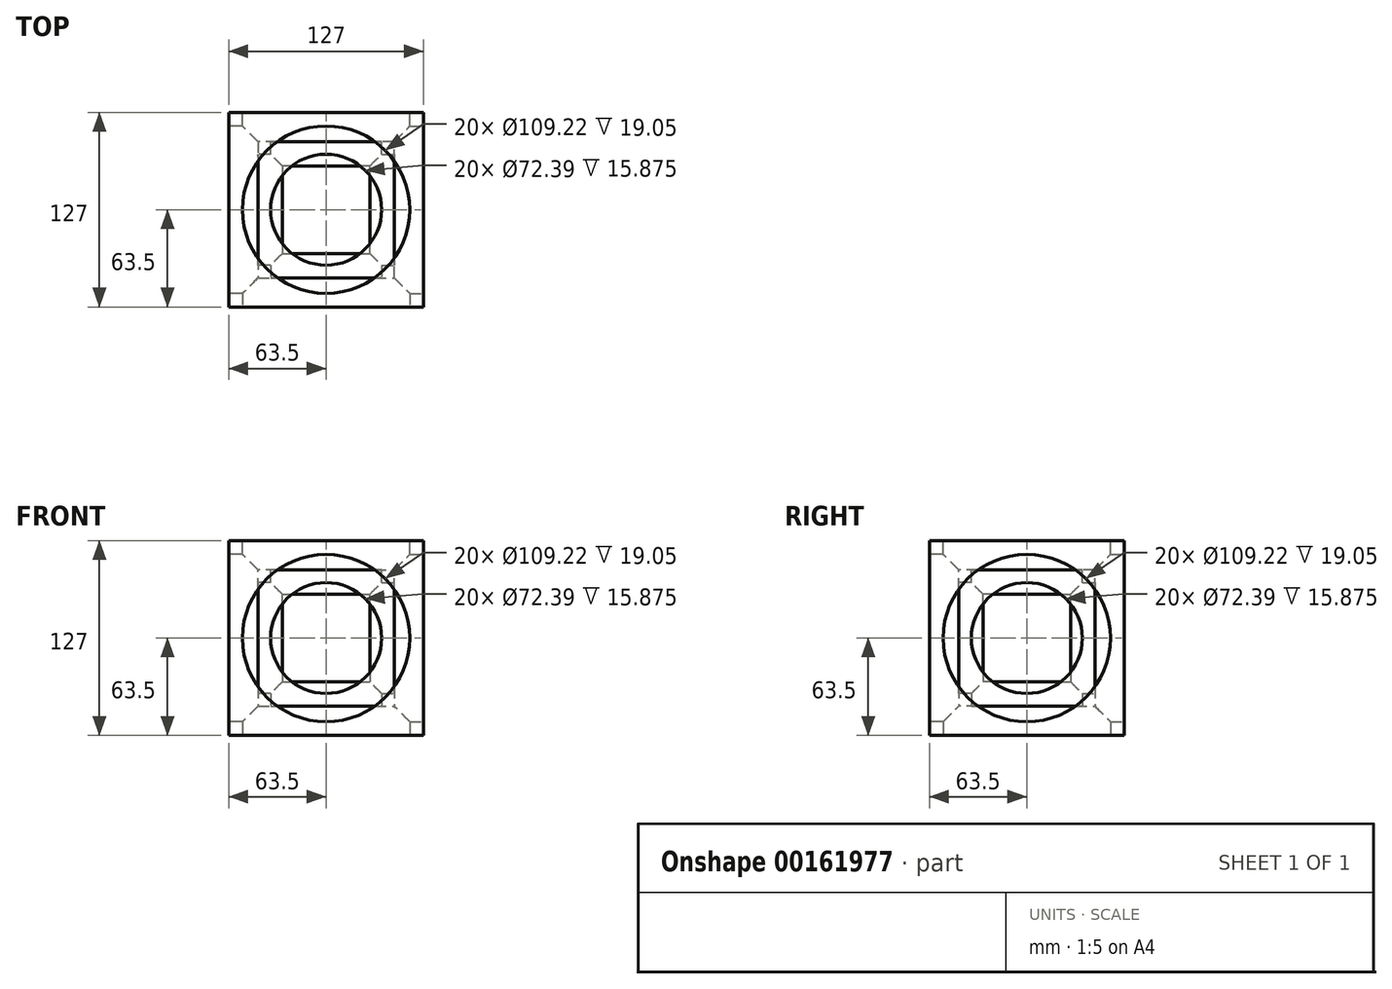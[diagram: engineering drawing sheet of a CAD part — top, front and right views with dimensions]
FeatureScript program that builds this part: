
annotation { "Feature Type Name" : "Feature", "Feature Type Description" : "" }
export const myFeature = defineFeature(function(context is Context, id is Id, definition is map)
    precondition{}
    {
        {
            var Q0;
            Q0=qCreatedBy(makeId("Top.planeOp"),FACE);
            var sketch = newSketch(context, id + "F15", { "sketchPlane" : qUnion([Q0])});
            skLineSegment(sketch, "E0.bottom", {"start": v(63.5, -63.5) * mm, "end": v(-63.5, -63.5) * mm});
            skLineSegment(sketch, "E0.top", {"start": v(63.5, 63.5) * mm, "end": v(-63.5, 63.5) * mm});
            skLineSegment(sketch, "E0.left", {"start": v(63.5, -63.5) * mm, "end": v(63.5, 63.5) * mm});
            skLineSegment(sketch, "E0.right", {"start": v(-63.5, -63.5) * mm, "end": v(-63.5, 63.5) * mm});
            skPoint(sketch, "E0.middle", {"position": v(0, 0) * mm});
            skSolve(sketch);
        }
        {
            var Q0;
            Q0=makeQuery(id+"F15.imprint","IMPRINT",FACE,{"disambiguationData":[TD([[makeQuery(id+"F15.imprint","IMPRINT",EDGE,{"derivedFrom":sQuery(id+"F15.wireOp",EDGE,"E0.bottom")}),-1.0]])]});
            extrude(context, id + "F16", {"entities" : qUnion([Q0]), "depth" : 127 * mm});
        }
        {
            var Q0;
            Q0=makeQuery(id+"F16.opExtrude","CAP_FACE",FACE,{"disambiguationData":[OSD([sQuery(id+"F15.wireOp",EDGE,"E0.bottom"),sQuery(id+"F15.wireOp",EDGE,"E0.top"),sQuery(id+"F15.wireOp",EDGE,"E0.left"),sQuery(id+"F15.wireOp",EDGE,"E0.right")])],"isStart":false});
            var sketch = newSketch(context, id + "F0", { "sketchPlane" : qUnion([Q0])});
            skCircle(sketch, "E1", {"center": v(0, 0) * mm, "radius": 54.61 * mm});
            skSolve(sketch);
        }
        {
            var Q0;
            Q0=makeQuery(id+"F0.imprint","IMPRINT",FACE,{"disambiguationData":[TD([[makeQuery(id+"F0.imprint","IMPRINT",EDGE,{"derivedFrom":sQuery(id+"F0.wireOp",EDGE,"E1")}),1.0]])]});
            extrude(context, id + "F17", {"entities" : qUnion([Q0]), "operationType" : NewBodyOperationType.REMOVE, "oppositeDirection" : true, "depth" : 19.05 * mm});
        }
        {
            var Q0;
            Q0=makeQuery(id+"F16.opExtrude","SWEPT_FACE",FACE,{"disambiguationData":[OSD([sQuery(id+"F15.wireOp",EDGE,"E0.left")])]});
            var sketch = newSketch(context, id + "F18", { "sketchPlane" : qUnion([Q0])});
            skCircle(sketch, "E2", {"center": v(0, 63.5) * mm, "radius": 54.61 * mm});
            skSolve(sketch);
        }
        {
            var Q0;
            Q0 = qSketchRegion(id + "F18", true);
            extrude(context, id + "F1", {"entities" : qUnion([Q0]), "operationType" : NewBodyOperationType.REMOVE, "oppositeDirection" : true, "depth" : 19.05 * mm});
        }
        {
            var Q0;
            Q0=makeQuery(id+"F16.opExtrude","SWEPT_FACE",FACE,{"disambiguationData":[OSD([sQuery(id+"F15.wireOp",EDGE,"E0.top")])]});
            var sketch = newSketch(context, id + "F19", { "sketchPlane" : qUnion([Q0])});
            skCircle(sketch, "E3", {"center": v(0, 63.5) * mm, "radius": 54.61 * mm});
            skSolve(sketch);
        }
        {
            var Q0;
            Q0 = qSketchRegion(id + "F19", true);
            var Q1;
            Q1=makeQuery(id+"F19.imprint","IMPRINT",FACE,{"disambiguationData":[TD([[makeQuery(id+"F19.imprint","IMPRINT",EDGE,{"derivedFrom":sQuery(id+"F19.wireOp",EDGE,"E3")}),1.0]])]});
            extrude(context, id + "F2", {"entities" : qUnion([Q0, Q1]), "operationType" : NewBodyOperationType.REMOVE, "oppositeDirection" : true, "depth" : 19.05 * mm});
        }
        {
            var Q0;
            Q0=makeQuery(id+"F16.opExtrude","SWEPT_FACE",FACE,{"disambiguationData":[OSD([sQuery(id+"F15.wireOp",EDGE,"E0.bottom")])]});
            var sketch = newSketch(context, id + "F3", { "sketchPlane" : qUnion([Q0])});
            skCircle(sketch, "E4", {"center": v(0, 63.5) * mm, "radius": 54.61 * mm});
            skSolve(sketch);
        }
        {
            var Q0;
            Q0 = qSketchRegion(id + "F3", true);
            var Q1;
            Q1=makeQuery(id+"F3.imprint","IMPRINT",FACE,{"disambiguationData":[TD([[makeQuery(id+"F3.imprint","IMPRINT",EDGE,{"derivedFrom":sQuery(id+"F3.wireOp",EDGE,"E4")}),1.0]])]});
            extrude(context, id + "F4", {"entities" : qUnion([Q0, Q1]), "operationType" : NewBodyOperationType.REMOVE, "oppositeDirection" : true, "depth" : 19.05 * mm});
        }
        {
            var Q0;
            Q0=makeQuery(id+"F16.opExtrude","SWEPT_FACE",FACE,{"disambiguationData":[OSD([sQuery(id+"F15.wireOp",EDGE,"E0.right")])]});
            var sketch = newSketch(context, id + "F20", { "sketchPlane" : qUnion([Q0])});
            skCircle(sketch, "E5", {"center": v(0, 63.5) * mm, "radius": 54.61 * mm});
            skSolve(sketch);
        }
        {
            var Q0;
            Q0 = qSketchRegion(id + "F20", true);
            var Q1;
            Q1=makeQuery(id+"F20.imprint","IMPRINT",FACE,{"disambiguationData":[TD([[makeQuery(id+"F20.imprint","IMPRINT",EDGE,{"derivedFrom":sQuery(id+"F20.wireOp",EDGE,"E5")}),1.0]])]});
            extrude(context, id + "F5", {"entities" : qUnion([Q0, Q1]), "operationType" : NewBodyOperationType.REMOVE, "oppositeDirection" : true, "depth" : 19.05 * mm});
        }
        {
            var Q0;
            Q0=makeQuery(id+"F16.opExtrude","CAP_FACE",FACE,{"disambiguationData":[OSD([sQuery(id+"F15.wireOp",EDGE,"E0.bottom"),sQuery(id+"F15.wireOp",EDGE,"E0.top"),sQuery(id+"F15.wireOp",EDGE,"E0.left"),sQuery(id+"F15.wireOp",EDGE,"E0.right")])],"isStart":true});
            var sketch = newSketch(context, id + "F6", { "sketchPlane" : qUnion([Q0])});
            skCircle(sketch, "E6", {"center": v(0, 0) * mm, "radius": 54.6 * mm});
            skSolve(sketch);
        }
        {
            var Q0;
            Q0 = qSketchRegion(id + "F6", true);
            extrude(context, id + "F21", {"entities" : qUnion([Q0]), "operationType" : NewBodyOperationType.REMOVE, "oppositeDirection" : true, "depth" : 19.05 * mm});
        }
        {
            var Q0;
            Q0=makeQuery(id+"F17.boolean.opBoolean","COPY",FACE,{"derivedFrom":makeQuery(id+"F17.opExtrude","CAP_FACE",FACE,{"disambiguationData":[OSD([sQuery(id+"F0.wireOp",EDGE,"E1")])],"isStart":false})});
            var sketch = newSketch(context, id + "F22", { "sketchPlane" : qUnion([Q0])});
            skCircle(sketch, "E7", {"center": v(0, 0) * mm, "radius": 36.2 * mm});
            skSolve(sketch);
        }
        {
            var Q0;
            Q0 = qSketchRegion(id + "F22", true);
            var Q1;
            Q1=makeQuery(id+"F22.imprint","IMPRINT",FACE,{"disambiguationData":[TD([[makeQuery(id+"F22.imprint","IMPRINT",EDGE,{"derivedFrom":sQuery(id+"F22.wireOp",EDGE,"E7")}),1.0]])]});
            extrude(context, id + "F7", {"entities" : qUnion([Q0, Q1]), "operationType" : NewBodyOperationType.REMOVE, "oppositeDirection" : true, "depth" : 15.88 * mm});
        }
        {
            var Q0;
            Q0=makeQuery(id+"F5.boolean.opBoolean","COPY",FACE,{"derivedFrom":makeQuery(id+"F5.opExtrude","CAP_FACE",FACE,{"disambiguationData":[OSD([sQuery(id+"F20.wireOp",EDGE,"E5")])],"isStart":false})});
            var sketch = newSketch(context, id + "F8", { "sketchPlane" : qUnion([Q0])});
            skCircle(sketch, "E8", {"center": v(0, 63.5) * mm, "radius": 36.2 * mm});
            skSolve(sketch);
        }
        {
            var Q0;
            Q0 = qSketchRegion(id + "F8", true);
            extrude(context, id + "F9", {"entities" : qUnion([Q0]), "operationType" : NewBodyOperationType.REMOVE, "oppositeDirection" : true, "depth" : 15.88 * mm});
        }
        {
            var Q0;
            Q0=makeQuery(id+"F1.boolean.opBoolean","COPY",FACE,{"derivedFrom":makeQuery(id+"F1.opExtrude","CAP_FACE",FACE,{"disambiguationData":[OSD([sQuery(id+"F18.wireOp",EDGE,"E2")])],"isStart":false})});
            var sketch = newSketch(context, id + "F23", { "sketchPlane" : qUnion([Q0])});
            skCircle(sketch, "E9", {"center": v(0, 63.5) * mm, "radius": 36.2 * mm});
            skSolve(sketch);
        }
        {
            var Q0;
            Q0 = qSketchRegion(id + "F23", true);
            extrude(context, id + "F10", {"entities" : qUnion([Q0]), "operationType" : NewBodyOperationType.REMOVE, "oppositeDirection" : true, "depth" : 15.88 * mm});
        }
        {
            var Q0;
            Q0=makeQuery(id+"F2.boolean.opBoolean","COPY",FACE,{"derivedFrom":makeQuery(id+"F2.opExtrude","CAP_FACE",FACE,{"disambiguationData":[OSD([sQuery(id+"F19.wireOp",EDGE,"E3")])],"isStart":false})});
            var sketch = newSketch(context, id + "F11", { "sketchPlane" : qUnion([Q0])});
            skCircle(sketch, "E10", {"center": v(0, 63.5) * mm, "radius": 36.2 * mm});
            skSolve(sketch);
        }
        {
            var Q0;
            Q0 = qSketchRegion(id + "F11", true);
            extrude(context, id + "F24", {"entities" : qUnion([Q0]), "operationType" : NewBodyOperationType.REMOVE, "oppositeDirection" : true, "depth" : 15.88 * mm});
        }
        {
            var Q0;
            Q0=makeQuery(id+"F4.boolean.opBoolean","COPY",FACE,{"derivedFrom":makeQuery(id+"F4.opExtrude","CAP_FACE",FACE,{"disambiguationData":[OSD([sQuery(id+"F3.wireOp",EDGE,"E4")])],"isStart":false})});
            var sketch = newSketch(context, id + "F25", { "sketchPlane" : qUnion([Q0])});
            skCircle(sketch, "E11", {"center": v(0, 63.5) * mm, "radius": 36.2 * mm});
            skSolve(sketch);
        }
        {
            var Q0;
            Q0 = qSketchRegion(id + "F25", true);
            extrude(context, id + "F12", {"entities" : qUnion([Q0]), "operationType" : NewBodyOperationType.REMOVE, "oppositeDirection" : true, "depth" : 15.88 * mm});
        }
        {
            var Q0;
            Q0=makeQuery(id+"F21.boolean.opBoolean","COPY",FACE,{"derivedFrom":makeQuery(id+"F21.opExtrude","CAP_FACE",FACE,{"disambiguationData":[OSD([sQuery(id+"F6.wireOp",EDGE,"E6")])],"isStart":false})});
            var sketch = newSketch(context, id + "F13", { "sketchPlane" : qUnion([Q0])});
            skCircle(sketch, "E12", {"center": v(0, 0) * mm, "radius": 36.2 * mm});
            skSolve(sketch);
        }
        {
            var Q0;
            Q0 = qSketchRegion(id + "F13", true);
            extrude(context, id + "F14", {"entities" : qUnion([Q0]), "operationType" : NewBodyOperationType.REMOVE, "oppositeDirection" : true, "depth" : 15.88 * mm});
        }
    });
